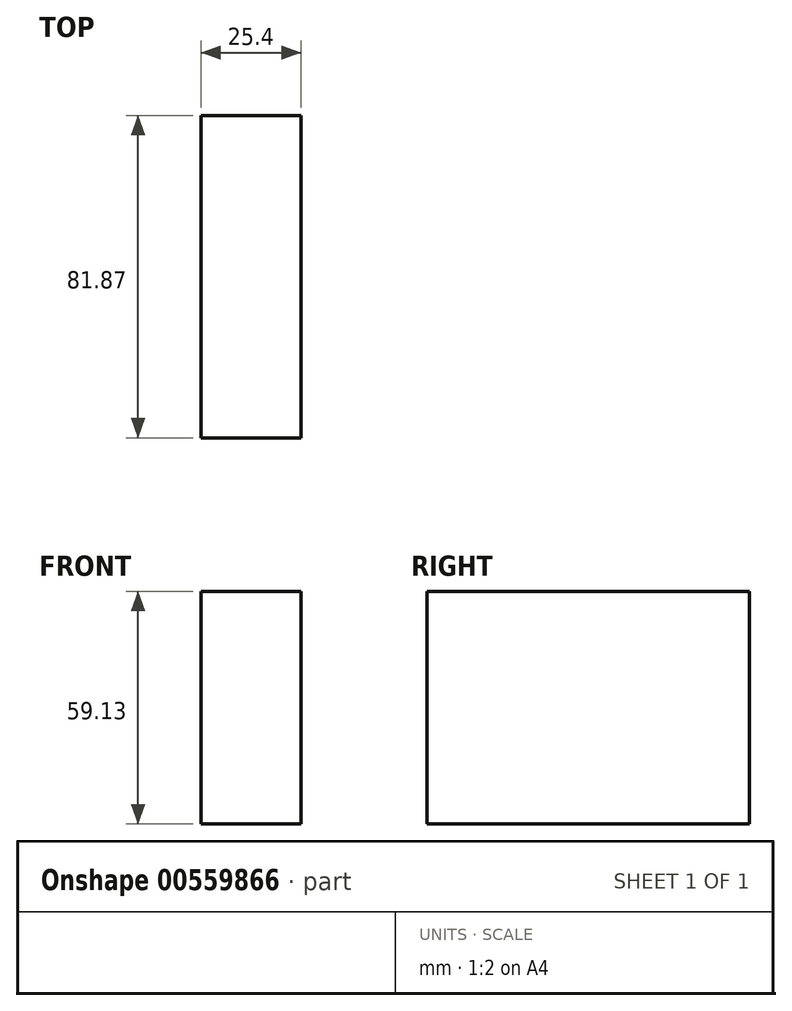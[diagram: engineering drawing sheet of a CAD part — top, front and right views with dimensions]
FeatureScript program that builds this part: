
annotation { "Feature Type Name" : "Feature", "Feature Type Description" : "" }
export const myFeature = defineFeature(function(context is Context, id is Id, definition is map)
    precondition{}
    {
        {
            var Q0;
            Q0=qCreatedBy(makeId("Right.planeOp"),FACE);
            var sketch = newSketch(context, id + "F0", { "sketchPlane" : qUnion([Q0])});
            skLineSegment(sketch, "E0.bottom", {"start": v(-39.42, 27.67) * mm, "end": v(42.45, 27.67) * mm});
            skLineSegment(sketch, "E0.top", {"start": v(-39.42, -31.46) * mm, "end": v(42.45, -31.46) * mm});
            skLineSegment(sketch, "E0.left", {"start": v(-39.42, 27.67) * mm, "end": v(-39.42, -31.46) * mm});
            skLineSegment(sketch, "E0.right", {"start": v(42.45, 27.67) * mm, "end": v(42.45, -31.46) * mm});
            skSolve(sketch);
        }
        {
            var Q0;
            Q0 = qSketchRegion(id + "F0", true);
            extrude(context, id + "F1", {"entities" : qUnion([Q0]), "depth" : 25.4 * mm, "offsetDistance" : 25.4 * mm});
        }
    });
